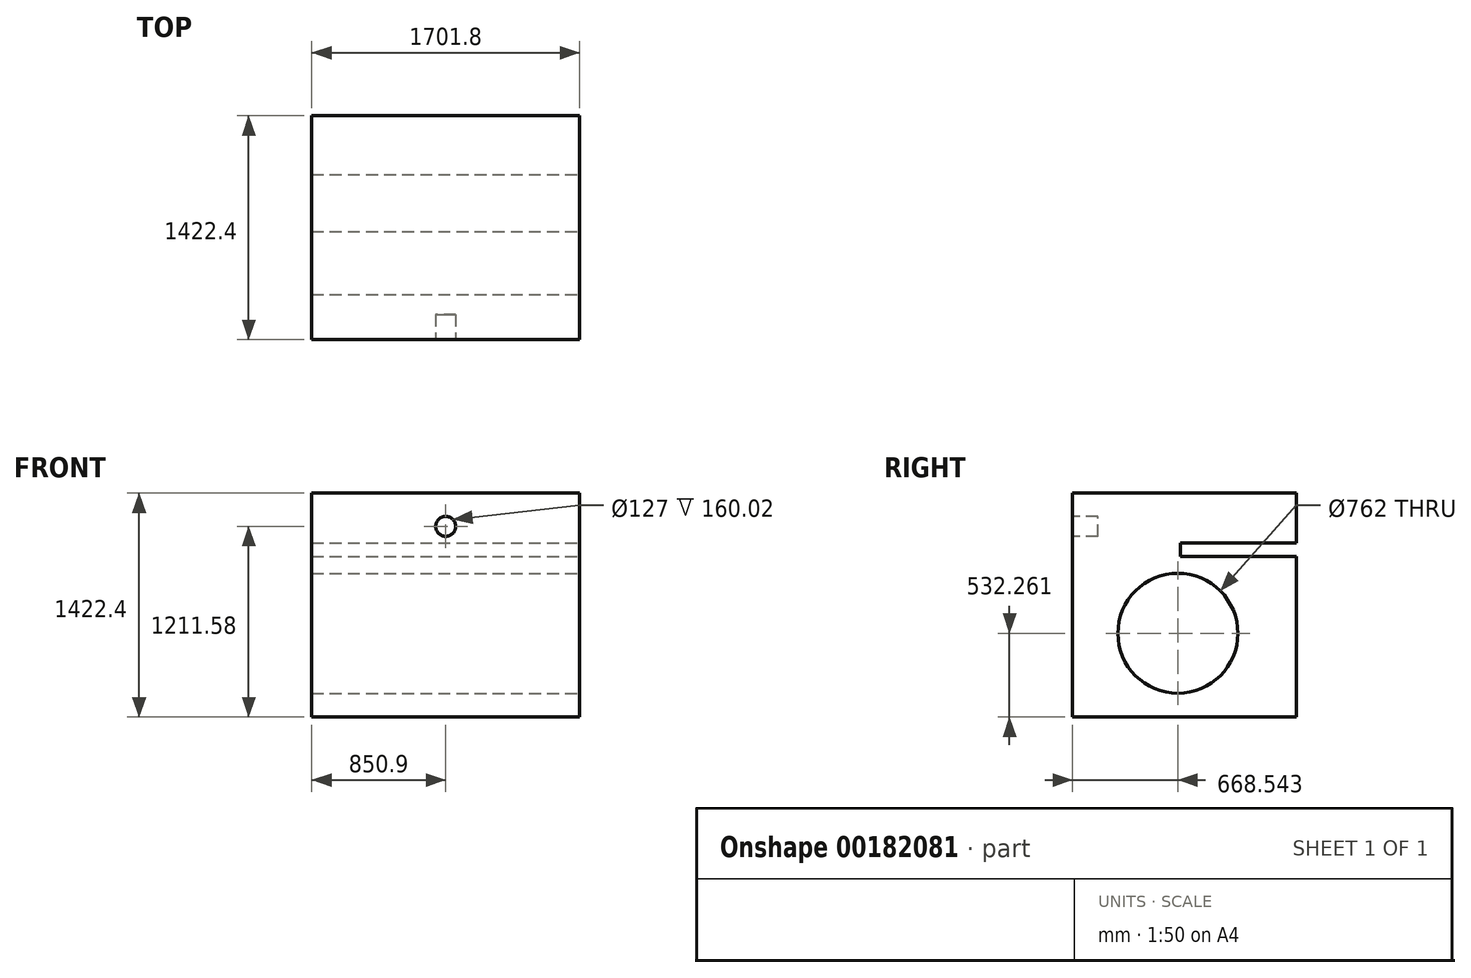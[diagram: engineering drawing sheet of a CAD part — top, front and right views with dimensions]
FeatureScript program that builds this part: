
annotation { "Feature Type Name" : "Feature", "Feature Type Description" : "" }
export const myFeature = defineFeature(function(context is Context, id is Id, definition is map)
    precondition{}
    {
        {
            var Q0;
            Q0=qCreatedBy(makeId("Front.planeOp"),FACE);
            var sketch = newSketch(context, id + "F0", { "sketchPlane" : qUnion([Q0])});
            skLineSegment(sketch, "E0.bottom", {"start": v(850.9, -711.2) * mm, "end": v(-850.9, -711.2) * mm});
            skLineSegment(sketch, "E0.top", {"start": v(850.9, 711.2) * mm, "end": v(-850.9, 711.2) * mm});
            skLineSegment(sketch, "E0.left", {"start": v(850.9, -711.2) * mm, "end": v(850.9, 711.2) * mm});
            skLineSegment(sketch, "E0.right", {"start": v(-850.9, -711.2) * mm, "end": v(-850.9, 711.2) * mm});
            skPoint(sketch, "E0.middle", {"position": v(0, 0) * mm});
            skSolve(sketch);
        }
        {
            var Q0;
            Q0 = qSketchRegion(id + "F0", true);
            extrude(context, id + "F1", {"entities" : qUnion([Q0]), "depth" : 1422.4 * mm});
        }
        {
            var Q0;
            Q0=makeQuery(id+"F1.opExtrude","CAP_FACE",FACE,{"disambiguationData":[OSD([sQuery(id+"F0.wireOp",EDGE,"E0.bottom"),sQuery(id+"F0.wireOp",EDGE,"E0.top"),sQuery(id+"F0.wireOp",EDGE,"E0.left"),sQuery(id+"F0.wireOp",EDGE,"E0.right")])],"isStart":false});
            var sketch = newSketch(context, id + "F2", { "sketchPlane" : qUnion([Q0])});
            skLineSegment(sketch, "E1", {"start": v(-850.9, 776.67) * mm, "end": v(0, 776.67) * mm});
            skLineSegment(sketch, "E2", {"start": v(0, 711.2) * mm, "end": v(0, 500.38) * mm});
            skCircle(sketch, "E3", {"center": v(0, 500.38) * mm, "radius": 63.5 * mm});
            skSolve(sketch);
        }
        {
            var Q0;
            Q0=makeQuery(id+"F2.imprint","IMPRINT",FACE,{"disambiguationData":[TD([[makeQuery(id+"F2.imprint","IMPRINT",EDGE,{"derivedFrom":sQuery(id+"F2.wireOp",EDGE,"E3")}),1.0]])]});
            extrude(context, id + "F3", {"entities" : qUnion([Q0]), "operationType" : NewBodyOperationType.REMOVE, "oppositeDirection" : true, "depth" : 160.02 * mm});
        }
        {
            var Q0;
            Q0=makeQuery(id+"F1.opExtrude","SWEPT_FACE",FACE,{"disambiguationData":[OSD([sQuery(id+"F0.wireOp",EDGE,"E0.left")])]});
            var sketch = newSketch(context, id + "F4", { "sketchPlane" : qUnion([Q0])});
            skLineSegment(sketch, "E4", {"start": v(87.77, 711.2) * mm, "end": v(87.77, 393.7) * mm});
            skLineSegment(sketch, "E5", {"start": v(87.77, 393.7) * mm, "end": v(87.77, 309.88) * mm});
            skLineSegment(sketch, "E6.bottom", {"start": v(0, 393.7) * mm, "end": v(-736.6, 393.7) * mm});
            skLineSegment(sketch, "E6.top", {"start": v(0, 309.88) * mm, "end": v(-736.6, 309.88) * mm});
            skLineSegment(sketch, "E6.left", {"start": v(0, 393.7) * mm, "end": v(0, 309.88) * mm});
            skLineSegment(sketch, "E6.right", {"start": v(-736.6, 393.7) * mm, "end": v(-736.6, 309.88) * mm});
            skSolve(sketch);
        }
        {
            var Q0;
            Q0 = qSketchRegion(id + "F4", true);
            extrude(context, id + "F5", {"entities" : qUnion([Q0]), "operationType" : NewBodyOperationType.REMOVE, "oppositeDirection" : true, "depth" : 1701.8 * mm});
        }
        {
            var Q0;
            Q0=makeQuery(id+"F1.opExtrude","SWEPT_FACE",FACE,{"disambiguationData":[OSD([sQuery(id+"F0.wireOp",EDGE,"E0.left")])]});
            var sketch = newSketch(context, id + "F6", { "sketchPlane" : qUnion([Q0])});
            skLineSegment(sketch, "E7", {"start": v(-1422.4, -711.2) * mm, "end": v(-1422.4, -25.4) * mm});
            skCircle(sketch, "E8", {"center": v(-753.86, -178.94) * mm, "radius": 381 * mm});
            skSolve(sketch);
        }
        {
            var Q0;
            Q0 = qSketchRegion(id + "F6", true);
            extrude(context, id + "F7", {"entities" : qUnion([Q0]), "operationType" : NewBodyOperationType.REMOVE, "oppositeDirection" : true, "depth" : 3035.3 * mm});
        }
    });
